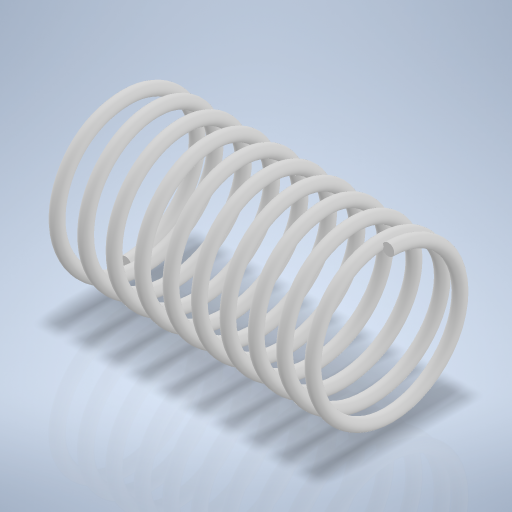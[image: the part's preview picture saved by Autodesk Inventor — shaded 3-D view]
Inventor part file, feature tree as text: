
AUTODESK INVENTOR PART (.ipt)
format: ipt  version: 2024 (Build 280153000, 153)  size: 911,360 bytes
history: native  units: mm
features: other x1, sketch x1
ambient origin geometry x8: Origin, YZ Plane, XZ Plane, XY Plane, X Axis, Y Axis, Z Axis, Center Point
bodies: Volumenkörper1 (feature_tree)
feature tree (2):
  other  "Spirale1"
  sketch  "Skizze1"  dims[d0=11.0mm d1=6.0mm d2=0.5mm d3=10.0mm d4=11.0mm d5=90.0mm d6=0.0mm d7=90.0deg d8=180.0deg d9=90.0deg d10=180.0deg]
